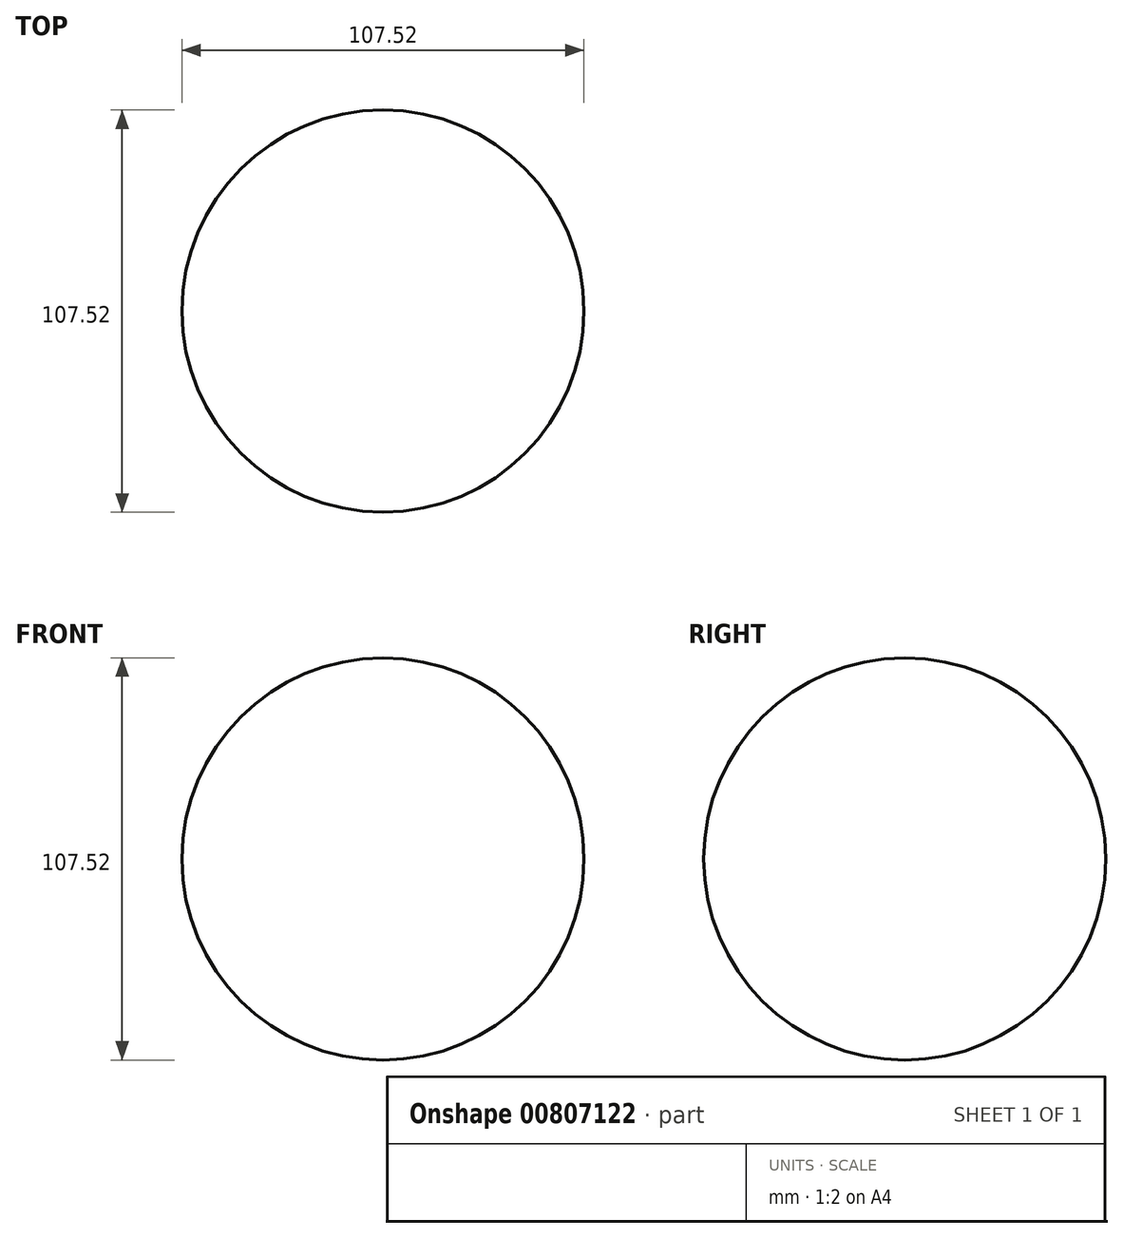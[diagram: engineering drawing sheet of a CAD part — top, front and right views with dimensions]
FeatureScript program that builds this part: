
annotation { "Feature Type Name" : "Feature", "Feature Type Description" : "" }
export const myFeature = defineFeature(function(context is Context, id is Id, definition is map)
    precondition{}
    {
        {
            var Q0;
            Q0=qCreatedBy(makeId("Right.planeOp"),FACE);
            var sketch = newSketch(context, id + "F0", { "sketchPlane" : qUnion([Q0])});
            skCircle(sketch, "E0", {"center": v(0, 0) * mm, "radius": 53.76 * mm});
            skLineSegment(sketch, "E1", {"start": v(0, 53.76) * mm, "end": v(0, -53.76) * mm});
            skSolve(sketch);
        }
        {
            var Q0;
            {var subQ0=sQuery(id+"F0.wireOp",EDGE,"E1");Q0=makeQuery(id+"F0.imprint","IMPRINT",FACE,{"disambiguationData":[TD([[makeQuery(id+"F0.imprint","IMPRINT",EDGE,{"derivedFrom":subQ0}),1.0]])]});}
            var Q1;
            Q1=sQuery(id+"F0.wireOp",EDGE,"E1");
            revolve(context, id + "F1", {"surfaceOperationType" : NewSurfaceOperationType.NEW, "entities" : qUnion([Q0]), "axis" : qUnion([Q1]), "revolveType" : RevolveType.FULL});
        }
    });
